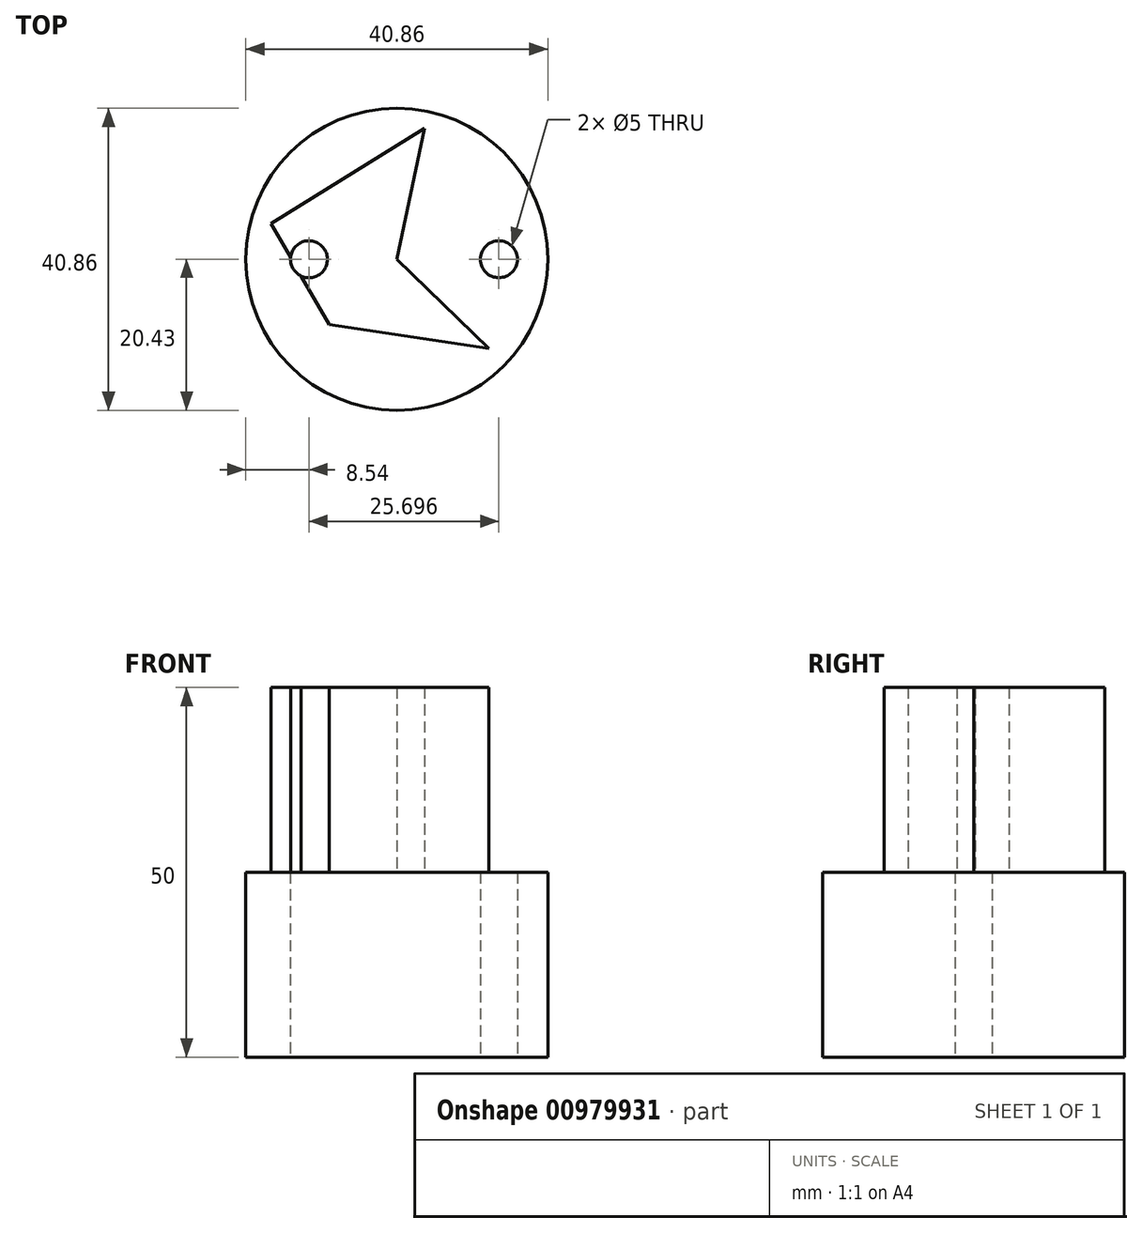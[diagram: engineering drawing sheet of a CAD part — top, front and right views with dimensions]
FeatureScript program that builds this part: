
annotation { "Feature Type Name" : "Feature", "Feature Type Description" : "" }
export const myFeature = defineFeature(function(context is Context, id is Id, definition is map)
    precondition{}
    {
        {
            var Q0;
            Q0=qCreatedBy(makeId("Top.planeOp"),FACE);
            var sketch = newSketch(context, id + "F0", { "sketchPlane" : qUnion([Q0])});
            skCircle(sketch, "E0", {"center": v(0, 0) * mm, "radius": 20.43 * mm});
            skSolve(sketch);
        }
        {
            var Q0;
            Q0 = qSketchRegion(id + "F0", true);
            extrude(context, id + "F1", {"entities" : qUnion([Q0]), "depth" : 25 * mm, "offsetDistance" : 25 * mm});
        }
        {
            var Q0;
            Q0=makeQuery(id+"F1.opExtrude","CAP_FACE",FACE,{"disambiguationData":[OSD([sQuery(id+"F0.wireOp",EDGE,"E0")])],"isStart":false});
            var sketch = newSketch(context, id + "F2", { "sketchPlane" : qUnion([Q0])});
            skLineSegment(sketch, "E1", {"start": v(14.64, -14.25) * mm, "end": v(0, 0) * mm});
            skLineSegment(sketch, "E2", {"start": v(0, 0) * mm, "end": v(3.72, 17.73) * mm});
            skLineSegment(sketch, "E3", {"start": v(3.72, 17.73) * mm, "end": v(-17.02, 4.8) * mm});
            skLineSegment(sketch, "E4", {"start": v(-17.02, 4.8) * mm, "end": v(-9.16, -8.86) * mm});
            skLineSegment(sketch, "E5", {"start": v(-9.16, -8.86) * mm, "end": v(12.6, -12.12) * mm});
            skLineSegment(sketch, "E6", {"start": v(12.6, -12.12) * mm, "end": v(14.64, -14.25) * mm});
            skSolve(sketch);
        }
        {
            var Q0;
            {var subQ1=sQuery(id+"F2.wireOp",EDGE,"E2");Q0=makeQuery(id+"F2.imprint","IMPRINT",FACE,{"disambiguationData":[TD([[makeQuery(id+"F2.imprint","IMPRINT",EDGE,{"derivedFrom":subQ1}),1.0]])]});}
            extrude(context, id + "F3", {"entities" : qUnion([Q0]), "operationType" : NewBodyOperationType.ADD, "depth" : 25 * mm, "offsetDistance" : 25 * mm});
        }
        {
            var Q0;
            Q0=makeQuery(id+"F1.opExtrude","CAP_FACE",FACE,{"disambiguationData":[OSD([sQuery(id+"F0.wireOp",EDGE,"E0")])],"isStart":true});
            var sketch = newSketch(context, id + "F4", { "sketchPlane" : qUnion([Q0])});
            skLineSegment(sketch, "E7", {"start": v(-11.9, 0) * mm, "end": v(13.8, 0) * mm});
            skSolve(sketch);
        }
        {
            var Q0;
            Q0=sQuery(id+"F4.wireOp",VERTEX,"E7.start");
            var Q1;
            Q1=sQuery(id+"F4.wireOp",VERTEX,"E7.end");
            var Q2;
            Q2=makeQuery(id+"F1.opExtrude","SWEPT_BODY",BODY,{"disambiguationData":[OSD([sQuery(id+"F0.wireOp",EDGE,"E0")])]});
            hole(context, id + "F5", {"style" : HoleStyle.SIMPLE, "endStyle" : HoleEndStyle.THROUGH, "holeDiameter" : 5 * mm, "majorDiameter" : 5 * mm, "isTappedThrough" : true, "tappedDepth" : 12 * mm, "tapClearance" : 3, "locations" : qUnion([Q0, Q1]), "scope" : qUnion([Q2])});
        }
    });
